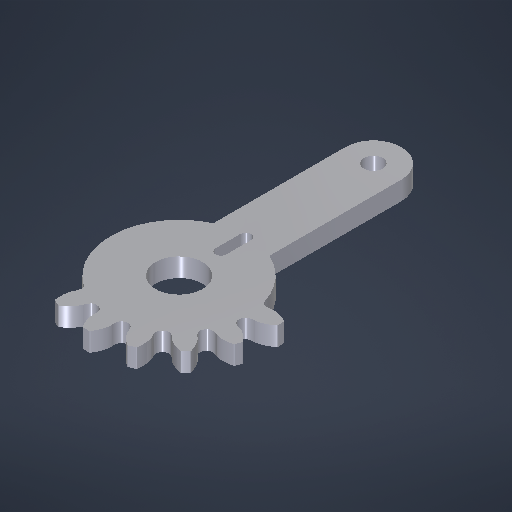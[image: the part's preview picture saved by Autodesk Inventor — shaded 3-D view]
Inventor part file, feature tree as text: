
AUTODESK INVENTOR PART (.ipt)
format: ipt  version: 2025.3 (Build 293356000, 356)  size: 532,480 bytes
history: native  units: mm
features: extrude x8, sketch x4, fillet x2, pattern_circular x1
ambient origin geometry x8: Origin, YZ Plane, XZ Plane, XY Plane, X Axis, Y Axis, Z Axis, Center Point
bodies: Solid1 (feature_tree)
feature tree (15):
  extrude  "Extrusion1"  TaperAngle=0.0deg  [1 undecoded]
  extrude  "Extrusion2"  Depth=10.0mm
  fillet  "Fillet1"  Radius=150.0mm
  pattern_circular  "Circular Pattern1"  [2 undecoded]
  extrude  "Extrusion8"  Depth=10.0mm TaperAngle=0.0deg
  extrude  "Extrusion9"  Depth=10.0mm TaperAngle=0.0deg
  extrude  "Extrusion11"  Depth=10.0mm
  fillet  "Fillet8"  Radius=31.1mm
  extrude  "Extrusion12"  Depth=4.5mm
  extrude  "Extrusion13"  Depth=10.0mm TaperAngle=0.0deg
  extrude  "Extrusion14"  Depth=10.0mm TaperAngle=0.0deg
  sketch  "Sketch9"  dims[d0=3.0mm d1=0.0mm]
  sketch  "Sketch13"  dims[d2=10.0mm d3=0.0mm d4=0.2mm d5=150.0mm d6=360.0deg]
  sketch  "Sketch14"  dims[d38=3.0mm]
  sketch  "Sketch15"  dims[d39=35.6mm d40=0.0mm d41=7.51mm d42=40.0mm d43=0.0mm d52=10.0mm d53=0.0mm d54=3.0mm d55=31.1mm d56=4.5mm d57=10.0mm d58=0.0mm d59=10.0mm d60=0.0mm d62=1.7mm d64=10.0mm d65=0.0mm]
note: 3 required parameter values undecoded (feature->parameter linkage not recoverable at this tier; creation-order binding heuristic only, values carry confidence <= 0.55)
